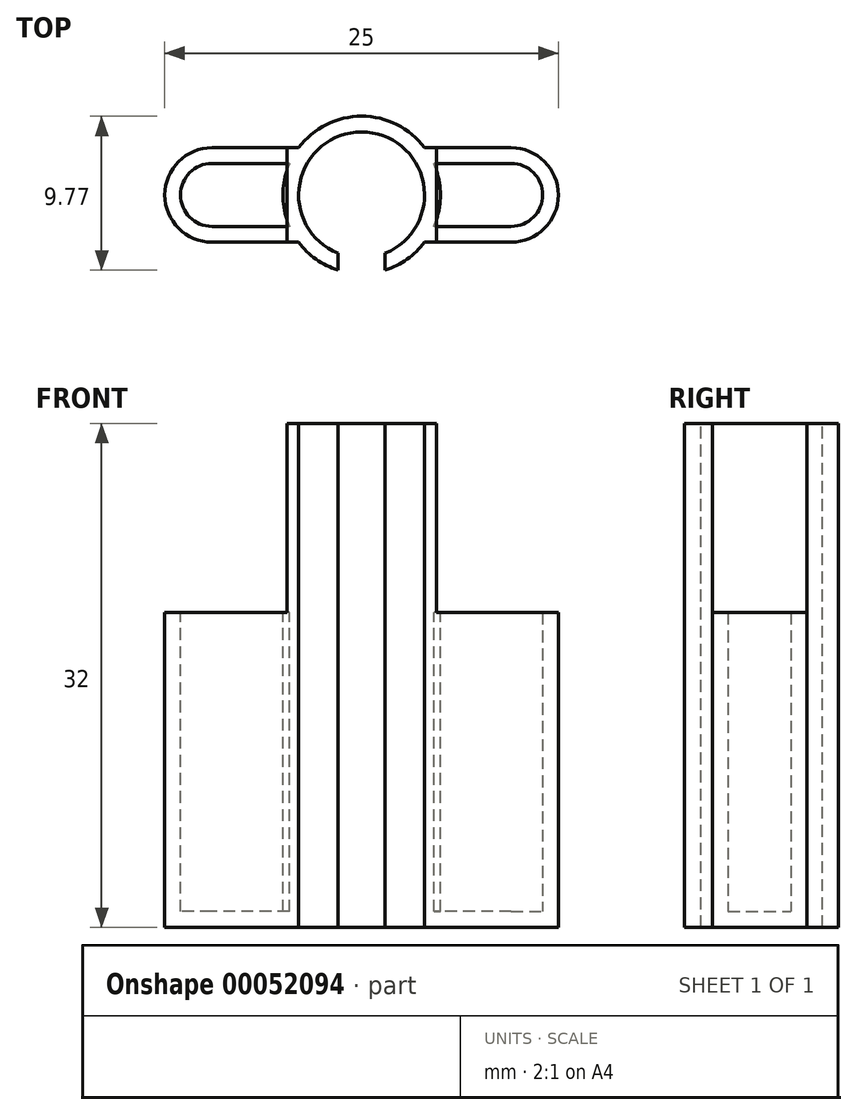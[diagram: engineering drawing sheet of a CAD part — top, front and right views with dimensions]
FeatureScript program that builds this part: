
annotation { "Feature Type Name" : "Feature", "Feature Type Description" : "" }
export const myFeature = defineFeature(function(context is Context, id is Id, definition is map)
    precondition{}
    {
        {
            var Q0;
            Q0=qCreatedBy(makeId("Top.planeOp"),FACE);
            var sketch = newSketch(context, id + "F0", { "sketchPlane" : qUnion([Q0])});
            skLineSegment(sketch, "E0.rect.bottom", {"start": v(12.5, 3) * mm, "end": v(-12.5, 3) * mm});
            skLineSegment(sketch, "E0.rect.top", {"start": v(12.5, -3) * mm, "end": v(-12.5, -3) * mm});
            skLineSegment(sketch, "E0.rect.left", {"start": v(12.5, 3) * mm, "end": v(12.5, -3) * mm});
            skLineSegment(sketch, "E0.rect.right", {"start": v(-12.5, 3) * mm, "end": v(-12.5, -3) * mm});
            skPoint(sketch, "E0.rect.middle", {"position": v(0, 0) * mm});
            skCircle(sketch, "E1", {"center": v(0, 0) * mm, "radius": 5 * mm});
            skSolve(sketch);
        }
        {
            var Q0;
            Q0 = qSketchRegion(id + "F0", true);
            extrude(context, id + "F1", {"entities" : qUnion([Q0]), "depth" : 32 * mm});
        }
        {
            var Q0;
            Q0=makeQuery(id+"F1.opExtrude","CAP_FACE",FACE,{"disambiguationData":[OSD([sQuery(id+"F0.wireOp",EDGE,"E0.rect.bottom"),sQuery(id+"F0.wireOp",EDGE,"E0.rect.top"),sQuery(id+"F0.wireOp",EDGE,"E0.rect.left"),sQuery(id+"F0.wireOp",EDGE,"E0.rect.right"),sQuery(id+"F0.wireOp",EDGE,"E1")])],"isStart":false});
            var sketch = newSketch(context, id + "F2", { "sketchPlane" : qUnion([Q0])});
            skCircle(sketch, "E2", {"center": v(0, 0) * mm, "radius": 4 * mm});
            skLineSegment(sketch, "E3.rect.bottom", {"start": v(1.5, -1.31) * mm, "end": v(-1.5, -1.31) * mm});
            skLineSegment(sketch, "E3.rect.top", {"start": v(1.5, -8.69) * mm, "end": v(-1.5, -8.69) * mm});
            skLineSegment(sketch, "E3.rect.left", {"start": v(1.5, -1.31) * mm, "end": v(1.5, -8.69) * mm});
            skLineSegment(sketch, "E3.rect.right", {"start": v(-1.5, -1.31) * mm, "end": v(-1.5, -8.69) * mm});
            skPoint(sketch, "E3.rect.middle", {"position": v(0, -5) * mm});
            skSolve(sketch);
        }
        {
            var Q0;
            Q0 = qSketchRegion(id + "F2", true);
            extrude(context, id + "F3", {"entities" : qUnion([Q0]), "operationType" : NewBodyOperationType.REMOVE, "endBound" : BoundingType.THROUGH_ALL, "oppositeDirection" : true, "depth" : 25 * mm});
        }
        {
            var Q0;
            Q0=makeQuery(id+"F1.opExtrude","SWEPT_EDGE",EDGE,{"disambiguationData":[OSD([sQuery(id+"F0.wireOp",EDGE,"E0.rect.top"),sQuery(id+"F0.wireOp",EDGE,"E0.rect.left")])]});
            var Q1;
            Q1=makeQuery(id+"F1.opExtrude","SWEPT_EDGE",EDGE,{"disambiguationData":[OSD([sQuery(id+"F0.wireOp",EDGE,"E0.rect.bottom"),sQuery(id+"F0.wireOp",EDGE,"E0.rect.left")])]});
            var Q2;
            Q2=makeQuery(id+"F1.opExtrude","SWEPT_EDGE",EDGE,{"disambiguationData":[OSD([sQuery(id+"F0.wireOp",EDGE,"E0.rect.top"),sQuery(id+"F0.wireOp",EDGE,"E0.rect.right")])]});
            var Q3;
            Q3=makeQuery(id+"F1.opExtrude","SWEPT_EDGE",EDGE,{"disambiguationData":[OSD([sQuery(id+"F0.wireOp",EDGE,"E0.rect.bottom"),sQuery(id+"F0.wireOp",EDGE,"E0.rect.right")])]});
            fillet(context, id + "F4", {"entities" : qUnion([Q0, Q1, Q2, Q3]), "radius" : 3 * mm, "tangentPropagation" : true, "allowEdgeOverflow" : false});
        }
        {
            var Q0;
            Q0=makeQuery(id+"F1.opExtrude","CAP_FACE",FACE,{"disambiguationData":[OSD([sQuery(id+"F0.wireOp",EDGE,"E0.rect.bottom"),sQuery(id+"F0.wireOp",EDGE,"E0.rect.top"),sQuery(id+"F0.wireOp",EDGE,"E0.rect.left"),sQuery(id+"F0.wireOp",EDGE,"E0.rect.right"),sQuery(id+"F0.wireOp",EDGE,"E1")])],"isStart":false});
            var sketch = newSketch(context, id + "F5", { "sketchPlane" : qUnion([Q0])});
            skLineSegment(sketch, "E4.rect.bottom", {"start": v(-4.75, 7.53) * mm, "end": v(-14.25, 7.53) * mm});
            skLineSegment(sketch, "E4.rect.top", {"start": v(-4.75, -7.53) * mm, "end": v(-14.25, -7.53) * mm});
            skLineSegment(sketch, "E4.rect.left", {"start": v(-4.75, 7.53) * mm, "end": v(-4.75, -7.53) * mm});
            skLineSegment(sketch, "E4.rect.right", {"start": v(-14.25, 7.53) * mm, "end": v(-14.25, -7.53) * mm});
            skPoint(sketch, "E4.rect.middle", {"position": v(-9.5, 0) * mm});
            skLineSegment(sketch, "E5", {"start": v(0, 0) * mm, "end": v(0, 16.4) * mm, "construction": true});
            skLineSegment(sketch, "E6.MirrorCS", {"start": v(4.75, 7.53) * mm, "end": v(14.25, 7.53) * mm});
            skPoint(sketch, "E7.MirrorP", {"position": v(9.5, 0) * mm});
            skLineSegment(sketch, "E8.MirrorCS", {"start": v(4.75, -7.53) * mm, "end": v(14.25, -7.53) * mm});
            skLineSegment(sketch, "E9.MirrorCS", {"start": v(4.75, 7.53) * mm, "end": v(4.75, -7.53) * mm});
            skLineSegment(sketch, "E10.MirrorCS", {"start": v(14.25, 7.53) * mm, "end": v(14.25, -7.53) * mm});
            skSolve(sketch);
        }
        {
            var Q0;
            Q0 = qSketchRegion(id + "F5", true);
            extrude(context, id + "F6", {"entities" : qUnion([Q0]), "operationType" : NewBodyOperationType.REMOVE, "oppositeDirection" : true, "depth" : 12 * mm});
        }
        {
            var Q0;
            Q0=makeQuery(id+"F6.boolean.opBoolean","COPY",FACE,{"derivedFrom":makeQuery(id+"F6.opExtrude","CAP_FACE",FACE,{"disambiguationData":[OSD([sQuery(id+"F5.wireOp",EDGE,"E4.rect.bottom"),sQuery(id+"F5.wireOp",EDGE,"E4.rect.top"),sQuery(id+"F5.wireOp",EDGE,"E4.rect.left"),sQuery(id+"F5.wireOp",EDGE,"E4.rect.right")])],"isStart":false})});
            var Q1;
            Q1=makeQuery(id+"F6.boolean.opBoolean","COPY",FACE,{"derivedFrom":makeQuery(id+"F6.opExtrude","CAP_FACE",FACE,{"disambiguationData":[OSD([sQuery(id+"F5.wireOp",EDGE,"E6.MirrorCS"),sQuery(id+"F5.wireOp",EDGE,"E8.MirrorCS"),sQuery(id+"F5.wireOp",EDGE,"E9.MirrorCS"),sQuery(id+"F5.wireOp",EDGE,"E10.MirrorCS")])],"isStart":false})});
            shell(context, id + "F7", {"entities" : qUnion([Q0, Q1]), "thickness" : 1 * mm});
        }
    });
